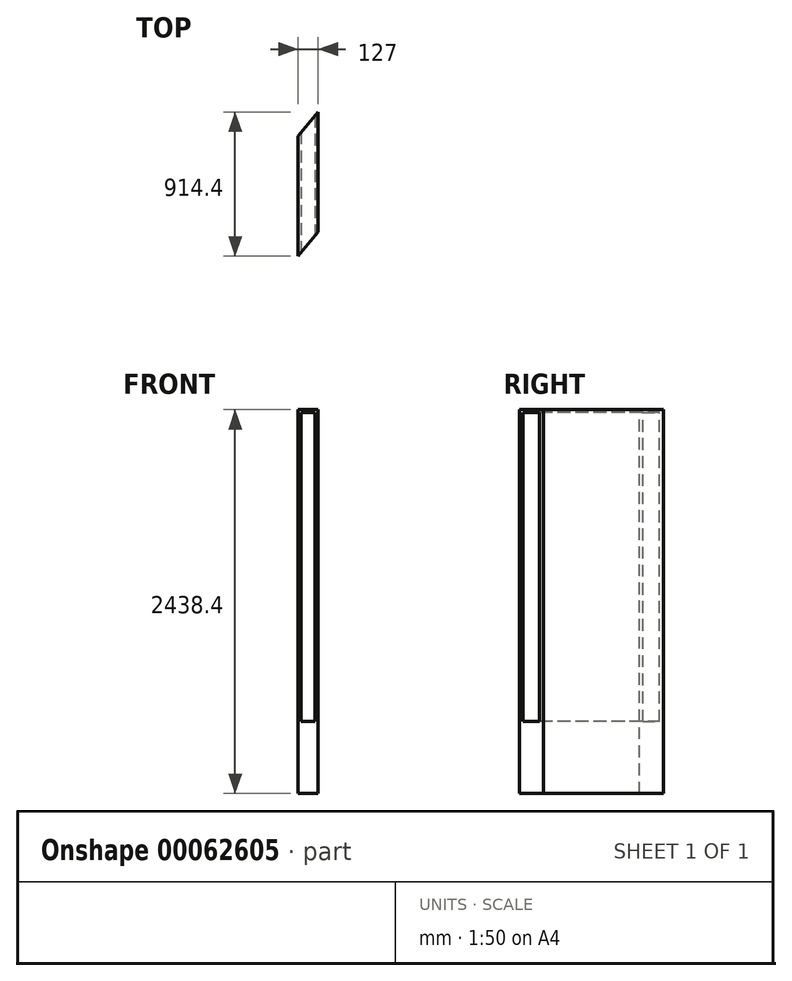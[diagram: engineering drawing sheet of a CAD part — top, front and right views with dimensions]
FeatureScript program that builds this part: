
annotation { "Feature Type Name" : "Feature", "Feature Type Description" : "" }
export const myFeature = defineFeature(function(context is Context, id is Id, definition is map)
    precondition{}
    {
        {
            var Q0;
            Q0=qCreatedBy(makeId("Right.planeOp"),FACE);
            var sketch = newSketch(context, id + "F0", { "sketchPlane" : qUnion([Q0])});
            skLineSegment(sketch, "E0.rect.bottom", {"start": v(457.2, 1219.2) * mm, "end": v(-457.2, 1219.2) * mm});
            skLineSegment(sketch, "E0.rect.top", {"start": v(457.2, -1219.2) * mm, "end": v(-457.2, -1219.2) * mm});
            skLineSegment(sketch, "E0.rect.left", {"start": v(457.2, 1219.2) * mm, "end": v(457.2, -1219.2) * mm});
            skLineSegment(sketch, "E0.rect.right", {"start": v(-457.2, 1219.2) * mm, "end": v(-457.2, -1219.2) * mm});
            skPoint(sketch, "E0.rect.middle", {"position": v(0, 0) * mm});
            skSolve(sketch);
        }
        {
            var Q0;
            Q0=qSketchRegion(id+"F0",true);
            extrude(context, id + "F1", {"entities" : qUnion([Q0]), "depth" : 127 * mm});
        }
        {
            var Q0;
            Q0=makeQuery(id+"F1.opExtrude","SWEPT_FACE",FACE,{"disambiguationData":[OSD([sQuery(id+"F0.wireOp",EDGE,"E0.rect.right")])]});
            var sketch = newSketch(context, id + "F2", { "sketchPlane" : qUnion([Q0])});
            skLineSegment(sketch, "E1.bottom", {"start": v(107.95, 1200.15) * mm, "end": v(19.05, 1200.15) * mm});
            skLineSegment(sketch, "E1.top", {"start": v(107.95, -762) * mm, "end": v(19.05, -762) * mm});
            skLineSegment(sketch, "E1.left", {"start": v(107.95, 1200.15) * mm, "end": v(107.95, -762) * mm});
            skLineSegment(sketch, "E1.right", {"start": v(19.05, 1200.15) * mm, "end": v(19.05, -762) * mm});
            skSolve(sketch);
        }
        {
            var Q0;
            Q0 = qSketchRegion(id + "F2", true);
            extrude(context, id + "F3", {"entities" : qUnion([Q0]), "operationType" : NewBodyOperationType.REMOVE, "endBound" : BoundingType.UP_TO_NEXT, "oppositeDirection" : true, "depth" : 25.4 * mm});
        }
        {
            var Q0;
            Q0=makeQuery(id+"F1.opExtrude","SWEPT_FACE",FACE,{"disambiguationData":[OSD([sQuery(id+"F0.wireOp",EDGE,"E0.rect.bottom")])]});
            var sketch = newSketch(context, id + "F4", { "sketchPlane" : qUnion([Q0])});
            skLineSegment(sketch, "E2", {"start": v(127, 457.2) * mm, "end": v(0, 457.2) * mm});
            skLineSegment(sketch, "E3", {"start": v(0, 457.2) * mm, "end": v(0, 304.8) * mm});
            skLineSegment(sketch, "E4", {"start": v(0, 304.8) * mm, "end": v(127, 457.2) * mm});
            skLineSegment(sketch, "E5", {"start": v(127, -304.8) * mm, "end": v(127, -457.2) * mm});
            skLineSegment(sketch, "E6", {"start": v(127, -457.2) * mm, "end": v(0, -457.2) * mm});
            skLineSegment(sketch, "E7", {"start": v(0, -457.2) * mm, "end": v(127, -304.8) * mm});
            skSolve(sketch);
        }
        {
            var Q0;
            Q0 = qSketchRegion(id + "F4", true);
            extrude(context, id + "F5", {"entities" : qUnion([Q0]), "operationType" : NewBodyOperationType.REMOVE, "endBound" : BoundingType.THROUGH_ALL, "oppositeDirection" : true, "depth" : 25.4 * mm});
        }
    });
